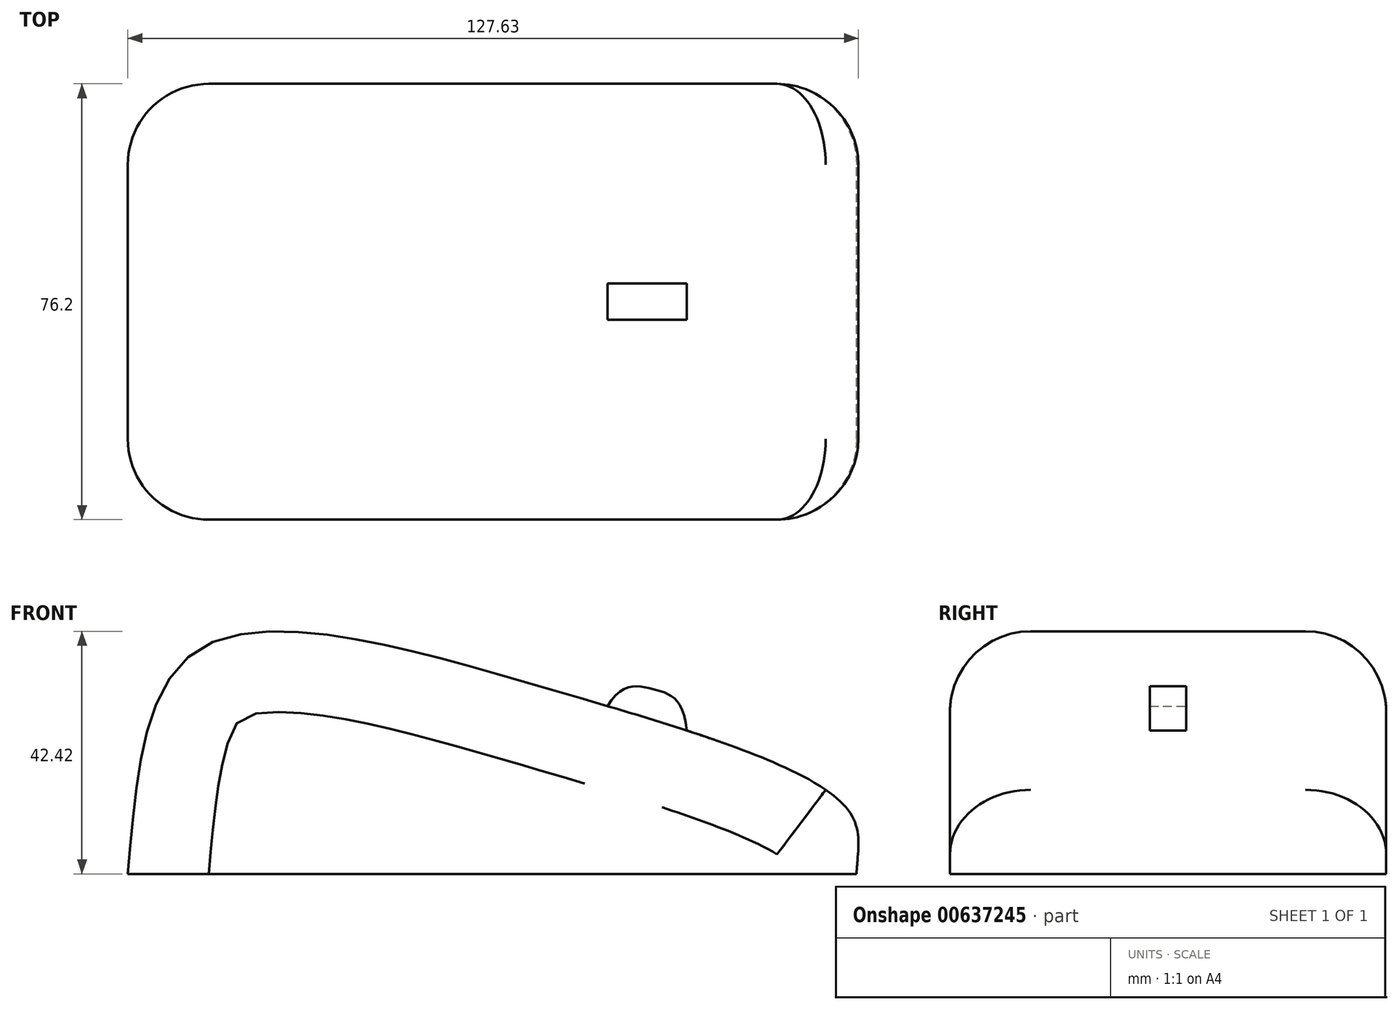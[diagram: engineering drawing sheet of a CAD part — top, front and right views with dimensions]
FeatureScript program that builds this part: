
annotation { "Feature Type Name" : "Feature", "Feature Type Description" : "" }
export const myFeature = defineFeature(function(context is Context, id is Id, definition is map)
    precondition{}
    {
        {
            var Q0;
            Q0=qCreatedBy(makeId("Front.planeOp"),FACE);
            var sketch = newSketch(context, id + "F0", { "sketchPlane" : qUnion([Q0])});
            skLineSegment(sketch, "E0", {"start": v(-64.86, 16.62) * mm, "end": v(62.43, 16.62) * mm});
            skFitSpline(sketch, "E1", {"points": [v(-64.86, 16.62) * mm, v(-52.66, 55.77) * mm, v(8.53, 49) * mm, v(60.94, 27.83) * mm, v(62.43, 16.62) * mm], "startDerivative": vector(16.89, 196.12) * mm, "endDerivative": vector(-5.86, -93.61) * mm});
            skFitSpline(sketch, "E2", {"points": [v(18.96, 45.95) * mm, v(27.14, 48.84) * mm, v(32.81, 41.67) * mm], "startDerivative": vector(15.78, 27) * mm, "endDerivative": vector(4.24, -35.12) * mm});
            skSolve(sketch);
        }
        {
            var Q0;
            {var subQ0=sQuery(id+"F0.wireOp",EDGE,"E0");Q0=makeQuery(id+"F0.imprint","IMPRINT",FACE,{"disambiguationData":[TD([[makeQuery(id+"F0.imprint","IMPRINT",EDGE,{"derivedFrom":subQ0}),1.0]])]});}
            extrude(context, id + "F1", {"entities" : qUnion([Q0]), "endBound" : BoundingType.SYMMETRIC, "depth" : 76.2 * mm, "offsetDistance" : 25.4 * mm});
        }
        {
            var Q0;
            {var subQ0=sQuery(id+"F0.wireOp",EDGE,"E2");Q0=makeQuery(id+"F0.imprint","IMPRINT",FACE,{"disambiguationData":[TD([[makeQuery(id+"F0.imprint","IMPRINT",EDGE,{"derivedFrom":subQ0}),-1.0]])]});}
            extrude(context, id + "F2", {"entities" : qUnion([Q0]), "operationType" : NewBodyOperationType.ADD, "endBound" : BoundingType.SYMMETRIC, "depth" : 6.35 * mm, "offsetDistance" : 25.4 * mm});
        }
        {
            var Q0;
            Q0=makeQuery(id+"F1.opExtrude","CAP_EDGE",EDGE,{"disambiguationData":[OSD([sQuery(id+"F0.wireOp",EDGE,"E1")])],"isStart":true});
            var Q1;
            Q1=makeQuery(id+"F1.opExtrude","CAP_EDGE",EDGE,{"disambiguationData":[OSD([sQuery(id+"F0.wireOp",EDGE,"E1")])],"isStart":false});
            fillet(context, id + "F3", {"entities" : qUnion([Q0, Q1]), "radius" : 14.1 * mm, "tangentPropagation" : true, "allowEdgeOverflow" : false});
        }
    });
